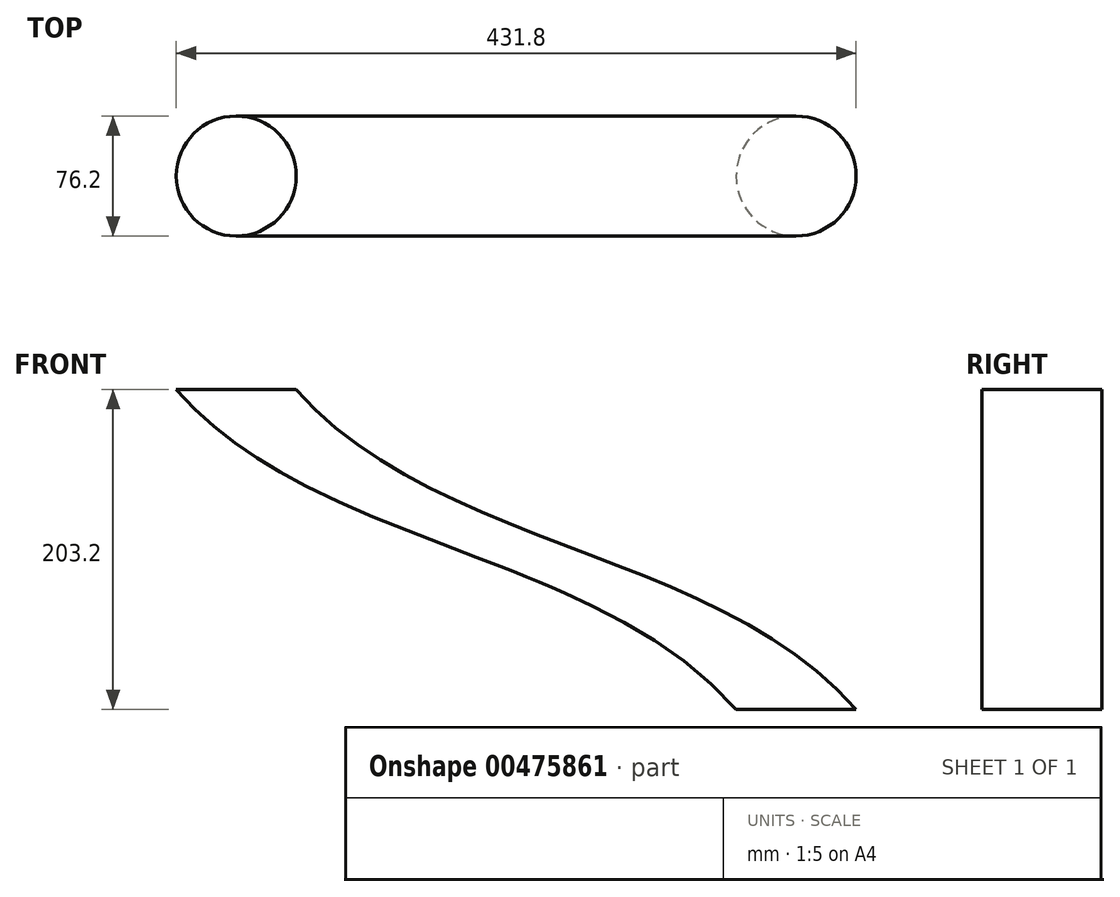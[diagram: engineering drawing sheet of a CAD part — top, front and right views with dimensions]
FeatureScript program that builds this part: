
annotation { "Feature Type Name" : "Feature", "Feature Type Description" : "" }
export const myFeature = defineFeature(function(context is Context, id is Id, definition is map)
    precondition{}
    {
        {
            var Q0;
            Q0=qCreatedBy(makeId("Top.planeOp"),FACE);
            var sketch = newSketch(context, id + "F0", { "sketchPlane" : qUnion([Q0])});
            skCircle(sketch, "E0", {"center": v(0, 0) * mm, "radius": 38.1 * mm});
            skSolve(sketch);
        }
        {
            var Q0;
            Q0=makeQuery(id+"F0.imprint","IMPRINT",FACE,{"disambiguationData":[TD([[makeQuery(id+"F0.imprint","IMPRINT",EDGE,{"derivedFrom":sQuery(id+"F0.wireOp",EDGE,"E0")}),1.0]])]});
            extrude(context, id + "F1", {"entities" : qUnion([Q0]), "depth" : 203.2 * mm});
        }
        {
            var Q0;
            Q0=qCreatedBy(makeId("Front.planeOp"),FACE);
            var sketch = newSketch(context, id + "F2", { "sketchPlane" : qUnion([Q0])});
            skLineSegment(sketch, "E1", {"start": v(0, 0) * mm, "end": v(38.1, 0) * mm});
            skFitSpline(sketch, "E2", {"points": [v(-317.5, 203.2) * mm, v(38.1, 0) * mm], "startDerivative": vector(266.7, -304.8) * mm, "endDerivative": vector(266.7, -304.8) * mm});
            skPoint(sketch, "E3.endSnap0", {"position": v(-139.7, 0) * mm});
            skLineSegment(sketch, "E4", {"start": v(-50.8, 101.6) * mm, "end": v(-50.8, 0) * mm});
            skFitSpline(sketch, "E5", {"points": [v(-317.5, 203.2) * mm, v(38.1, 0) * mm], "startDerivative": vector(533.4, -152.4) * mm, "endDerivative": vector(266.7, -304.8) * mm});
            skSolve(sketch);
        }
        {
            var Q0;
            Q0=makeQuery(id+"F1.opExtrude","CAP_FACE",FACE,{"disambiguationData":[OSD([sQuery(id+"F0.wireOp",EDGE,"E0")])],"isStart":false});
            var Q1;
            Q1=sQuery(id+"F2.wireOp",EDGE,"E2");
            sweep(context, id + "F3", {"profiles" : qUnion([Q0]), "path" : qUnion([Q1]), "keepProfileOrientation" : true});
        }
        {
            var Q0;
            Q0=makeQuery(id+"F1.opExtrude","SWEPT_BODY",BODY,{"disambiguationData":[OSD([sQuery(id+"F0.wireOp",EDGE,"E0")])]});
            deleteBodies(context, id + "F4", {"entities" : qUnion([Q0])});
        }
    });
